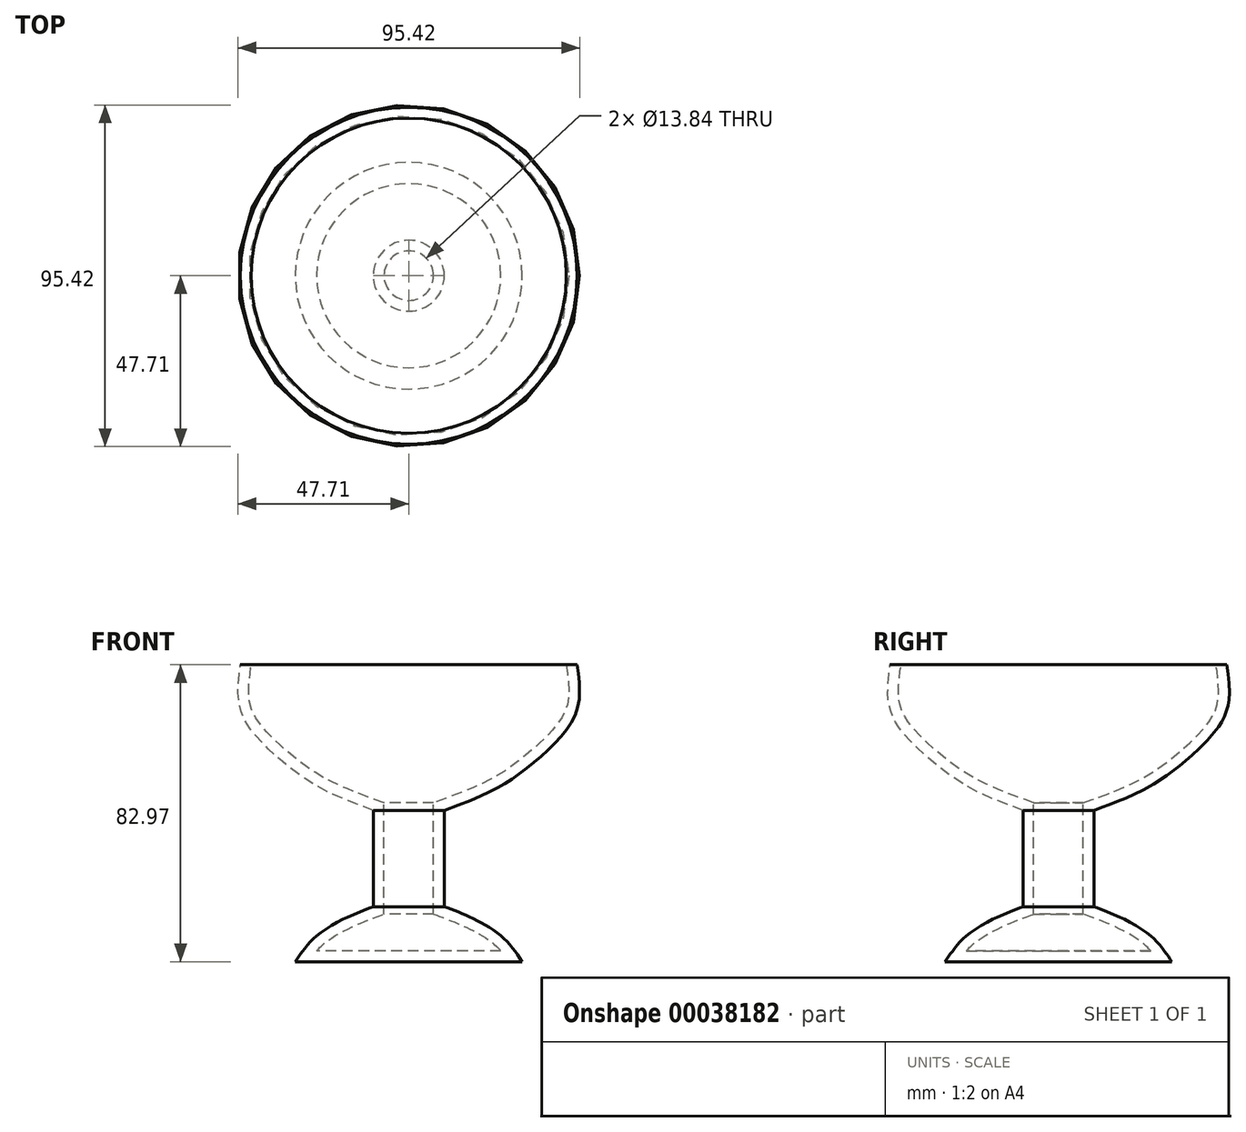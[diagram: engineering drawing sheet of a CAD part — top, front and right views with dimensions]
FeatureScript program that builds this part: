
annotation { "Feature Type Name" : "Feature", "Feature Type Description" : "" }
export const myFeature = defineFeature(function(context is Context, id is Id, definition is map)
    precondition{}
    {
        {
            var Q0;
            Q0=qCreatedBy(makeId("Front.planeOp"),FACE);
            var sketch = newSketch(context, id + "F0", { "sketchPlane" : qUnion([Q0])});
            skLineSegment(sketch, "E0", {"start": v(0, 37.17) * mm, "end": v(0, -45.8) * mm});
            skLineSegment(sketch, "E1", {"start": v(0, -45.8) * mm, "end": v(31.68, -45.8) * mm});
            skLineSegment(sketch, "E2", {"start": v(0, 37.17) * mm, "end": v(47.05, 37.17) * mm});
            skLineSegment(sketch, "E3", {"start": v(9.92, -3.51) * mm, "end": v(9.92, -30.42) * mm});
            skFitSpline(sketch, "E4", {"points": [v(47.05, 37.17) * mm, v(47.05, 24.68) * mm, v(39.68, 14.1) * mm, v(28.16, 4.82) * mm, v(9.92, -3.51) * mm], "startDerivative": vector(7.67, -56.6) * mm, "endDerivative": vector(-99.37, -36.36) * mm});
            skFitSpline(sketch, "E5", {"points": [v(9.92, -30.42) * mm, v(16.96, -33.3) * mm, v(25.92, -38.75) * mm, v(31.68, -45.8) * mm], "startDerivative": vector(22.03, -8.38) * mm, "endDerivative": vector(15.07, -22.18) * mm});
            skSolve(sketch);
        }
        {
            var Q0;
            Q0=makeQuery(id+"F0.imprint","IMPRINT",FACE,{"disambiguationData":[TD([[makeQuery(id+"F0.imprint","IMPRINT",EDGE,{"derivedFrom":sQuery(id+"F0.wireOp",EDGE,"E0")}),1.0]])]});
            var Q1;
            Q1=sQuery(id+"F0.wireOp",EDGE,"E0");
            revolve(context, id + "F1", {"entities" : qUnion([Q0]), "axis" : qUnion([Q1]), "revolveType" : RevolveType.FULL});
        }
        {
            var Q0;
            Q0=makeQuery(id+"F1.opRevolve","SWEPT_FACE",FACE,{"disambiguationData":[OSD([sQuery(id+"F0.wireOp",EDGE,"E2")])]});
            shell(context, id + "F2", {"entities" : qUnion([Q0]), "thickness" : 3 * mm});
        }
    });
